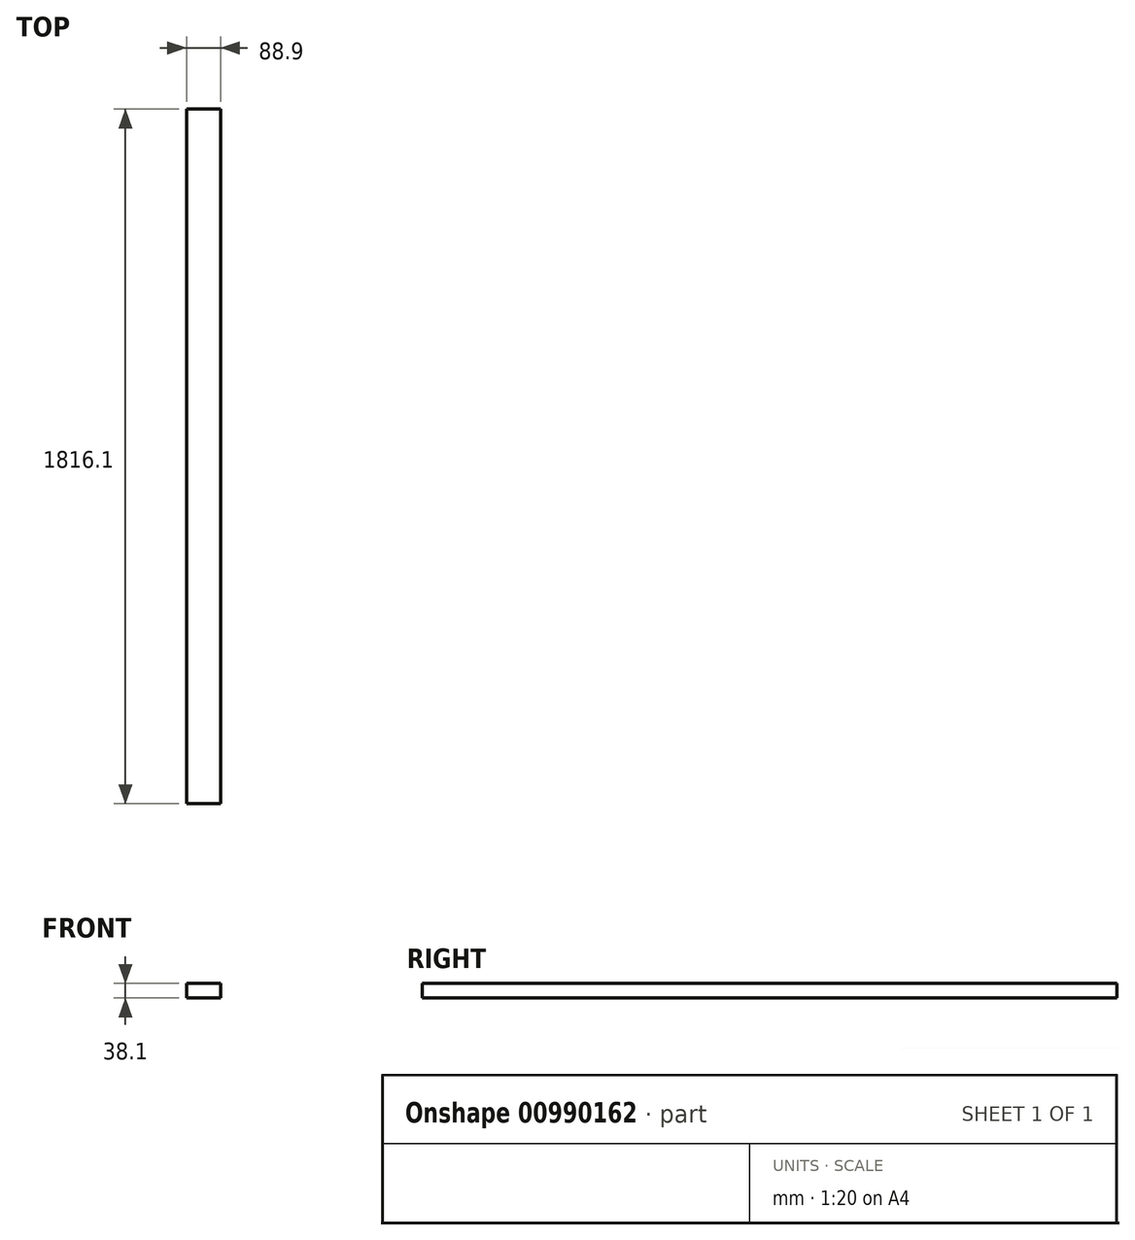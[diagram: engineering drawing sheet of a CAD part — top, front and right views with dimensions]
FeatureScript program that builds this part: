
annotation { "Feature Type Name" : "Feature", "Feature Type Description" : "" }
export const myFeature = defineFeature(function(context is Context, id is Id, definition is map)
    precondition{}
    {
        {
            assignVariable(context, id + "F0", {"name" : "w", "anyValue" : 38.1 * mm});
        }
        {
            var Q0;
            Q0=qCreatedBy(makeId("Top.planeOp"),FACE);
            var sketch = newSketch(context, id + "F1", { "sketchPlane" : qUnion([Q0])});
            skLineSegment(sketch, "E0.bottom", {"start": v(44.45, 908.05) * mm, "end": v(-44.45, 908.05) * mm});
            skLineSegment(sketch, "E0.top", {"start": v(44.45, -908.05) * mm, "end": v(-44.45, -908.05) * mm});
            skLineSegment(sketch, "E0.left", {"start": v(44.45, 908.05) * mm, "end": v(44.45, -908.05) * mm});
            skLineSegment(sketch, "E0.right", {"start": v(-44.45, 908.05) * mm, "end": v(-44.45, -908.05) * mm});
            skPoint(sketch, "E0.middle", {"position": v(0, 0) * mm});
            skSolve(sketch);
        }
        {
            var Q0;
            Q0=qSketchRegion(id+"F1",true);
            extrude(context, id + "F2", {"entities" : qUnion([Q0]), "depth" : getVariable(context, 'w'), "offsetDistance" : 25.4 * mm});
        }
    });
